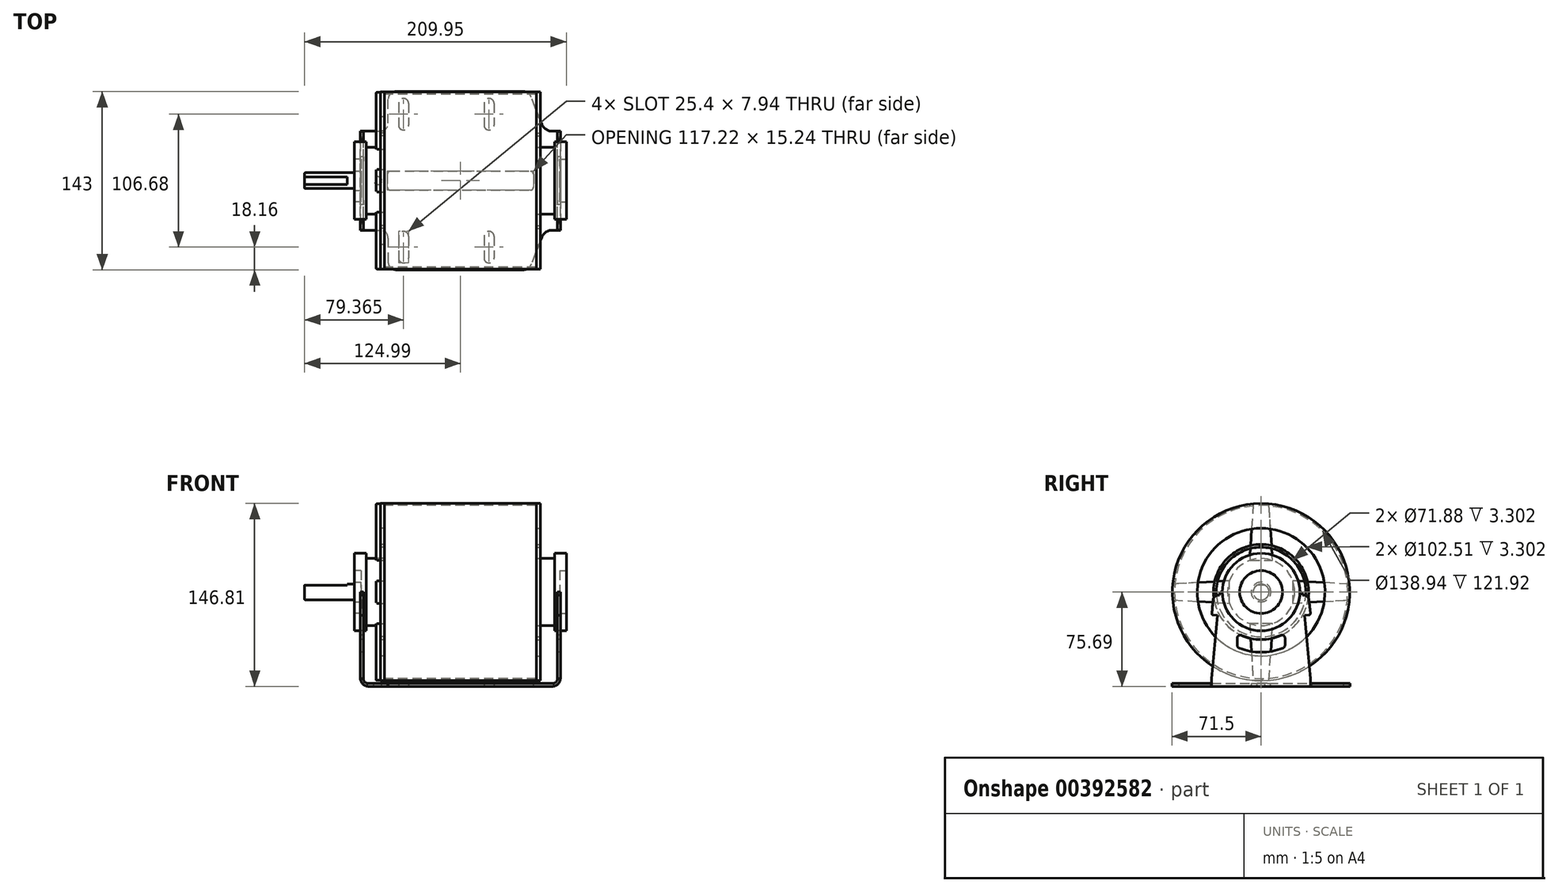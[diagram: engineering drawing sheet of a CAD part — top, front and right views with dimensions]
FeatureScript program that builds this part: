
annotation { "Feature Type Name" : "Feature", "Feature Type Description" : "" }
export const myFeature = defineFeature(function(context is Context, id is Id, definition is map)
    precondition{}
    {
        {
            var Q0;
            Q0=qCreatedBy(makeId("Right.planeOp"),FACE);
            var sketch = newSketch(context, id + "F0", { "sketchPlane" : qUnion([Q0])});
            skCircle(sketch, "E0", {"center": v(0, 0) * mm, "radius": 71.12 * mm});
            skCircle(sketch, "E1.0", {"center": v(0, 0) * mm, "radius": 69.47 * mm});
            skSolve(sketch);
        }
        {
            var Q0;
            Q0=makeQuery(id+"F0.imprint","IMPRINT",FACE,{"disambiguationData":[TD([[makeQuery(id+"F0.imprint","IMPRINT",EDGE,{"derivedFrom":sQuery(id+"F0.wireOp",EDGE,"E0")}),1.0]])]});
            extrude(context, id + "F1", {"entities" : qUnion([Q0]), "depth" : 121.92 * mm});
        }
        {
            var Q0;
            Q0=qCreatedBy(makeId("Front.planeOp"),FACE);
            var sketch = newSketch(context, id + "F2", { "sketchPlane" : qUnion([Q0])});
            skLineSegment(sketch, "E2", {"start": v(0, 0) * mm, "end": v(0, 71.12) * mm});
            skLineSegment(sketch, "E3", {"start": v(0, 71.12) * mm, "end": v(-3.3, 71.12) * mm});
            skLineSegment(sketch, "E4", {"start": v(-3.3, 71.12) * mm, "end": v(-3.3, 26.92) * mm});
            skLineSegment(sketch, "E5", {"start": v(-3.3, 26.92) * mm, "end": v(-14.48, 26.92) * mm});
            skLineSegment(sketch, "E6", {"start": v(-14.48, 26.92) * mm, "end": v(-14.48, 31.12) * mm});
            skLineSegment(sketch, "E7", {"start": v(-14.48, 31.12) * mm, "end": v(-24, 31.12) * mm});
            skLineSegment(sketch, "E8", {"start": v(-24, 31.12) * mm, "end": v(-24, 17.15) * mm});
            skLineSegment(sketch, "E9", {"start": v(-24, 17.15) * mm, "end": v(-18.67, 17.15) * mm});
            skLineSegment(sketch, "E10", {"start": v(-18.67, 17.15) * mm, "end": v(-18.67, 0) * mm});
            skLineSegment(sketch, "E11", {"start": v(-18.67, 0) * mm, "end": v(0, 0) * mm});
            skSolve(sketch);
        }
        {
            var Q0;
            Q0=makeQuery(id+"F2.imprint","IMPRINT",FACE,{"disambiguationData":[TD([[makeQuery(id+"F2.imprint","IMPRINT",EDGE,{"derivedFrom":sQuery(id+"F2.wireOp",EDGE,"E2")}),1.0]])]});
            var Q1;
            Q1=sQuery(id+"F2.wireOp",EDGE,"E11");
            revolve(context, id + "F3", {"entities" : qUnion([Q0]), "axis" : qUnion([Q1]), "revolveType" : RevolveType.FULL});
        }
        {
            var Q0;
            Q0=makeQuery(id+"F3.opRevolve","SWEPT_FACE",FACE,{"disambiguationData":[OSD([sQuery(id+"F2.wireOp",EDGE,"E4")])]});
            var sketch = newSketch(context, id + "F4", { "sketchPlane" : qUnion([Q0])});
            skCircle(sketch, "E12", {"center": v(0, 0) * mm, "radius": 51.26 * mm});
            skCircle(sketch, "E13", {"center": v(0, 0) * mm, "radius": 38.23 * mm});
            skCircle(sketch, "E14.0", {"center": v(0, 0) * mm, "radius": 35.94 * mm});
            skSolve(sketch);
        }
        {
            var Q0;
            Q0=qSketchRegion(id+"F4",true);
            var Q1;
            Q1=makeQuery(id+"F4.imprint","IMPRINT",FACE,{"disambiguationData":[TD([[makeQuery(id+"F4.imprint","IMPRINT",EDGE,{"derivedFrom":sQuery(id+"F4.wireOp",EDGE,"E14.0")}),1.0]])]});
            extrude(context, id + "F5", {"entities" : qUnion([Q0, Q1]), "operationType" : NewBodyOperationType.REMOVE, "endBound" : BoundingType.THROUGH_ALL, "oppositeDirection" : true, "depth" : 25.4 * mm});
        }
        {
            var Q0;
            Q0=qCreatedBy(makeId("Right.planeOp"),FACE);
            var sketch = newSketch(context, id + "F6", { "sketchPlane" : qUnion([Q0])});
            skLineSegment(sketch, "E15", {"start": v(0, 0) * mm, "end": v(0, 71.12) * mm, "construction": true});
            skPoint(sketch, "E16.rect.middle", {"position": v(0, 71.12) * mm});
            skCircle(sketch, "E17", {"center": v(0, 26.92) * mm, "radius": 9.2 * mm, "construction": true});
            skCircle(sketch, "E18.0", {"center": v(0, 0) * mm, "radius": 71.12 * mm, "construction": true});
            skCircle(sketch, "E19", {"center": v(0, 71.12) * mm, "radius": 6.35 * mm, "construction": true});
            skLineSegment(sketch, "E20", {"start": v(9.07, 25.35) * mm, "end": v(6.38, 70.83) * mm});
            skLineSegment(sketch, "E21", {"start": v(6.38, 70.83) * mm, "end": v(-6.38, 70.83) * mm});
            skLineSegment(sketch, "E22", {"start": v(-6.38, 70.83) * mm, "end": v(-9.07, 25.35) * mm});
            skLineSegment(sketch, "E23", {"start": v(-9.07, 25.35) * mm, "end": v(9.07, 25.35) * mm});
            skCircle(sketch, "E24.0", {"center": v(0, 0) * mm, "radius": 26.92 * mm, "construction": true});
            skSolve(sketch);
        }
        {
            var Q0;
            {var subQ3=sQuery(id+"F6.wireOp",EDGE,"E20");Q0=makeQuery(id+"F6.imprint","IMPRINT",FACE,{"disambiguationData":[TD([[makeQuery(id+"F6.imprint","IMPRINT",EDGE,{"derivedFrom":subQ3}),1.0]])]});}
            extrude(context, id + "F7", {"entities" : qUnion([Q0]), "oppositeDirection" : true, "depth" : 6.6 * mm});
        }
        {
            var Q0;
            Q0=makeQuery(id+"F7.opExtrude","CAP_EDGE",EDGE,{"disambiguationData":[OSD([sQuery(id+"F6.wireOp",EDGE,"E20")])],"isStart":false});
            var Q1;
            Q1=makeQuery(id+"F7.opExtrude","CAP_EDGE",EDGE,{"disambiguationData":[OSD([sQuery(id+"F6.wireOp",EDGE,"E21")])],"isStart":false});
            var Q2;
            Q2=makeQuery(id+"F7.opExtrude","CAP_EDGE",EDGE,{"disambiguationData":[OSD([sQuery(id+"F6.wireOp",EDGE,"E22")])],"isStart":false});
            var Q3;
            Q3=makeQuery(id+"F7.opExtrude","SWEPT_EDGE",EDGE,{"disambiguationData":[OSD([sQuery(id+"F2.wireOp",EDGE,"E3"),sQuery(id+"F2.wireOp",EDGE,"E4"),sQuery(id+"F6.wireOp",EDGE,"E20"),sQuery(id+"F6.wireOp",EDGE,"E21")])]});
            var Q4;
            Q4=makeQuery(id+"F7.opExtrude","SWEPT_EDGE",EDGE,{"disambiguationData":[OSD([sQuery(id+"F2.wireOp",EDGE,"E3"),sQuery(id+"F2.wireOp",EDGE,"E4"),sQuery(id+"F6.wireOp",EDGE,"E21"),sQuery(id+"F6.wireOp",EDGE,"E22")])]});
            fillet(context, id + "F8", {"entities" : qUnion([Q0, Q1, Q2, Q3, Q4]), "radius" : 0.5 * mm, "tangentPropagation" : true, "allowEdgeOverflow" : false});
        }
        {
            var Q0;
            Q0=makeQuery(id+"F7.opExtrude","SWEPT_BODY",BODY,{"disambiguationData":[OSD([sQuery(id+"F2.wireOp",EDGE,"E4"),sQuery(id+"F2.wireOp",EDGE,"E5"),sQuery(id+"F6.wireOp",EDGE,"E20"),sQuery(id+"F6.wireOp",EDGE,"E21"),sQuery(id+"F6.wireOp",EDGE,"E22")])]});
            var Q1;
            Q1=sQuery(id+"F2.wireOp",EDGE,"E11");
            circularPattern(context, id + "F9", {"entities" : qUnion([Q0]), "axis" : qUnion([Q1]), "angle" : 360 * degree, "instanceCount" : 4, "equalSpace" : true, "computeTransformsWithoutBuiltin" : true});
        }
        {
            var Q0;
            Q0=qCreatedBy(makeId("Right.planeOp"),FACE);
            cPlane(context, id + "F10", {"entities" : qUnion([Q0]), "cplaneType" : CPlaneType.OFFSET, "offset" : 60.96 * mm, "width" : 152.4 * mm, "height" : 152.4 * mm});
        }
        {
            var Q0;
            Q0=makeQuery(id+"F5.boolean.opBoolean","SPLIT",BODY,{"disambiguationData":[OD(0.0)],"derivedFrom":makeQuery(id+"F3.opRevolve","SWEPT_BODY",BODY,{"disambiguationData":[OSD([sQuery(id+"F2.wireOp",EDGE,"E2"),sQuery(id+"F2.wireOp",EDGE,"E3"),sQuery(id+"F2.wireOp",EDGE,"E4"),sQuery(id+"F2.wireOp",EDGE,"E5"),sQuery(id+"F2.wireOp",EDGE,"E6"),sQuery(id+"F2.wireOp",EDGE,"E7"),sQuery(id+"F2.wireOp",EDGE,"E8"),sQuery(id+"F2.wireOp",EDGE,"E9"),sQuery(id+"F2.wireOp",EDGE,"E10"),sQuery(id+"F2.wireOp",EDGE,"E11")])]})});
            var Q1;
            Q1=qCreatedBy(id+"F10.planeOp",FACE);
            mirror(context, id + "F11", {"entities" : qUnion([Q0]), "mirrorPlane" : qUnion([Q1])});
        }
        {
            var Q0;
            Q0=qCreatedBy(makeId("Front.planeOp"),FACE);
            var sketch = newSketch(context, id + "F12", { "sketchPlane" : qUnion([Q0])});
            skLineSegment(sketch, "E25.0.0", {"start": v(-18.67, -17.15) * mm, "end": v(-18.67, 17.15) * mm, "construction": true});
            skLineSegment(sketch, "E26", {"start": v(-18.67, 0) * mm, "end": v(-64.03, 0) * mm});
            skLineSegment(sketch, "E27", {"start": v(-64.03, 0) * mm, "end": v(-64.03, 5.84) * mm});
            skLineSegment(sketch, "E28", {"start": v(-63.53, 6.35) * mm, "end": v(-23.75, 6.35) * mm});
            skLineSegment(sketch, "E29", {"start": v(-23.24, 7.89) * mm, "end": v(-18.67, 7.89) * mm});
            skLineSegment(sketch, "E30", {"start": v(-18.67, 7.89) * mm, "end": v(-18.67, 0) * mm});
            skLineSegment(sketch, "E31", {"start": v(-23.75, 7.38) * mm, "end": v(-23.75, 6.35) * mm});
            skPoint(sketch, "E32.visualSharp", {"position": v(-23.75, 7.89) * mm});
            skArc(sketch, "E32.filletArc", {"start": v(-23.24, 7.89) * mm, "mid": v(-23.6, 7.74) * mm, "end": v(-23.75, 7.38) * mm});
            skPoint(sketch, "E33.visualSharp", {"position": v(-64.03, 6.35) * mm});
            skArc(sketch, "E33.filletArc", {"start": v(-63.53, 6.35) * mm, "mid": v(-63.88, 6.2) * mm, "end": v(-64.03, 5.84) * mm});
            skSolve(sketch);
        }
        {
            var Q0;
            Q0=makeQuery(id+"F12.imprint","IMPRINT",FACE,{"disambiguationData":[TD([[makeQuery(id+"F12.imprint","IMPRINT",EDGE,{"derivedFrom":sQuery(id+"F12.wireOp",EDGE,"E26")}),-1.0]])]});
            var Q1;
            Q1=sQuery(id+"F12.wireOp",EDGE,"E26");
            revolve(context, id + "F13", {"entities" : qUnion([Q0]), "axis" : qUnion([Q1]), "revolveType" : RevolveType.FULL});
        }
        {
            var Q0;
            Q0=makeQuery(id+"F13.opRevolve","SWEPT_FACE",FACE,{"disambiguationData":[OSD([sQuery(id+"F12.wireOp",EDGE,"E27")])]});
            var sketch = newSketch(context, id + "F14", { "sketchPlane" : qUnion([Q0])});
            skCircle(sketch, "E34.0", {"center": v(0, 0) * mm, "radius": 6.35 * mm});
            skLineSegment(sketch, "E35", {"start": v(-6.6, -6.35) * mm, "end": v(6.6, -6.35) * mm, "construction": true});
            skLineSegment(sketch, "E36", {"start": v(0, -6.35) * mm, "end": v(0, 6.35) * mm, "construction": true});
            skLineSegment(sketch, "E37.0", {"start": v(-3.02, 5.59) * mm, "end": v(3.02, 5.59) * mm});
            skSolve(sketch);
        }
        {
            var Q0;
            {var subQ0=makeQuery(id+"F13.opRevolve","SWEPT_EDGE",EDGE,{"disambiguationData":[OSD([sQuery(id+"F12.wireOp",EDGE,"E27"),sQuery(id+"F12.wireOp",EDGE,"E33.filletArc")])]});var subQ1=sQuery(id+"F14.wireOp",EDGE,"E37.0");var subQ3=makeQuery(id+"F14.imprint","INTERSECT",VERTEX,{"disambiguationData":[OD(0.0)],"derivedFrom":[subQ0,subQ1]});Q0=makeQuery(id+"F14.imprint","IMPRINT",FACE,{"disambiguationData":[TD([[makeQuery(id+"F14.imprint","IMPRINT",EDGE,{"disambiguationData":[TD([[subQ3,-1.0]])],"derivedFrom":subQ1}),1.0]])]});}
            var Q1;
            {var subQ1=sQuery(id+"F14.wireOp",EDGE,"E37.0");var subQ4=sQuery(id+"F14.wireOp",EDGE,"E34.0");var subQ6=makeQuery(id+"F14.imprint","INTERSECT",VERTEX,{"disambiguationData":[OD(0.0)],"derivedFrom":[subQ4,subQ1]});Q1=makeQuery(id+"F14.imprint","IMPRINT",FACE,{"disambiguationData":[TD([[makeQuery(id+"F14.imprint","IMPRINT",EDGE,{"disambiguationData":[TD([[subQ6,1.0]])],"derivedFrom":subQ4}),1.0]])]});}
            extrude(context, id + "F15", {"entities" : qUnion([Q0, Q1]), "operationType" : NewBodyOperationType.REMOVE, "oppositeDirection" : true, "depth" : 34.04 * mm});
        }
        {
            var Q0;
            Q0=qCreatedBy(makeId("Front.planeOp"),FACE);
            var sketch = newSketch(context, id + "F16", { "sketchPlane" : qUnion([Q0])});
            skLineSegment(sketch, "E38", {"start": v(-154.25, 0) * mm, "end": v(252.33, 0) * mm, "construction": true});
            skLineSegment(sketch, "E39", {"start": v(-12.9, -75.7) * mm, "end": v(134.81, -75.7) * mm});
            skLineSegment(sketch, "E40", {"start": v(-24, 31.12) * mm, "end": v(-14.48, 31.12) * mm, "construction": true});
            skLineSegment(sketch, "E41", {"start": v(136.4, 31.12) * mm, "end": v(145.92, 31.12) * mm, "construction": true});
            skLineSegment(sketch, "E42", {"start": v(-19.24, 31.12) * mm, "end": v(-19.24, 0) * mm, "construction": true});
            skLineSegment(sketch, "E43", {"start": v(141.16, 31.12) * mm, "end": v(141.16, 0) * mm, "construction": true});
            skLineSegment(sketch, "E44", {"start": v(-19.24, 0) * mm, "end": v(-19.24, -69.34) * mm});
            skLineSegment(sketch, "E45", {"start": v(141.16, 0) * mm, "end": v(141.16, -69.34) * mm});
            skPoint(sketch, "E46.visualSharp", {"position": v(-19.24, -75.7) * mm});
            skArc(sketch, "E46.filletArc", {"start": v(-19.24, -69.34) * mm, "mid": v(-17.38, -73.83) * mm, "end": v(-12.9, -75.7) * mm});
            skPoint(sketch, "E47.visualSharp", {"position": v(141.16, -75.7) * mm});
            skArc(sketch, "E47.filletArc", {"start": v(134.81, -75.7) * mm, "mid": v(139.3, -73.83) * mm, "end": v(141.16, -69.34) * mm});
            skLineSegment(sketch, "E48.0", {"start": v(138.87, 0) * mm, "end": v(138.87, -69.34) * mm});
            skArc(sketch, "E48.1", {"start": v(134.81, -73.4) * mm, "mid": v(137.68, -72.22) * mm, "end": v(138.87, -69.34) * mm});
            skLineSegment(sketch, "E48.2", {"start": v(-12.9, -73.4) * mm, "end": v(134.81, -73.4) * mm});
            skArc(sketch, "E48.3", {"start": v(-16.95, -69.34) * mm, "mid": v(-15.76, -72.22) * mm, "end": v(-12.9, -73.4) * mm});
            skLineSegment(sketch, "E48.4", {"start": v(-16.95, 0) * mm, "end": v(-16.95, -69.34) * mm});
            skLineSegment(sketch, "E49", {"start": v(-19.24, 0) * mm, "end": v(-16.95, 0) * mm});
            skLineSegment(sketch, "E50", {"start": v(138.87, 0) * mm, "end": v(141.16, 0) * mm});
            skSolve(sketch);
        }
        {
            var Q0;
            Q0=qSketchRegion(id+"F16",true);
            extrude(context, id + "F17", {"entities" : qUnion([Q0]), "depth" : 79.5 * mm, "symmetric" : true});
        }
        {
            var Q0;
            Q0=qCreatedBy(makeId("Top.planeOp"),FACE);
            cPlane(context, id + "F18", {"entities" : qUnion([Q0]), "cplaneType" : CPlaneType.OFFSET, "offset" : 75.7 * mm, "oppositeDirection" : true, "width" : 152.4 * mm, "height" : 152.4 * mm});
        }
        {
            var Q0;
            Q0=qCreatedBy(id+"F18.planeOp",FACE);
            var sketch = newSketch(context, id + "F19", { "sketchPlane" : qUnion([Q0])});
            skLineSegment(sketch, "E51.0", {"start": v(-19.24, -39.75) * mm, "end": v(-12.9, -39.75) * mm, "construction": true});
            skLineSegment(sketch, "E52.0", {"start": v(-19.24, 39.75) * mm, "end": v(-12.9, 39.75) * mm, "construction": true});
            skLineSegment(sketch, "E53.bottom", {"start": v(15.34, 66.04) * mm, "end": v(15.34, 66.04) * mm});
            skLineSegment(sketch, "E53.top", {"start": v(15.34, 40.64) * mm, "end": v(15.34, 40.64) * mm});
            skLineSegment(sketch, "E53.left", {"start": v(11.37, 62.07) * mm, "end": v(11.37, 44.6) * mm});
            skLineSegment(sketch, "E53.right", {"start": v(19.3, 62.07) * mm, "end": v(19.3, 44.6) * mm});
            skPoint(sketch, "E54.visualSharp", {"position": v(11.37, 66.04) * mm});
            skArc(sketch, "E54.filletArc", {"start": v(15.34, 66.04) * mm, "mid": v(12.53, 64.88) * mm, "end": v(11.37, 62.07) * mm});
            skPoint(sketch, "E55.visualSharp", {"position": v(19.3, 66.04) * mm});
            skArc(sketch, "E55.filletArc", {"start": v(19.3, 62.07) * mm, "mid": v(18.14, 64.88) * mm, "end": v(15.34, 66.04) * mm});
            skPoint(sketch, "E56.visualSharp", {"position": v(19.3, 40.64) * mm});
            skArc(sketch, "E56.filletArc", {"start": v(15.34, 40.64) * mm, "mid": v(18.14, 41.8) * mm, "end": v(19.3, 44.6) * mm});
            skPoint(sketch, "E57.visualSharp", {"position": v(11.37, 40.64) * mm});
            skArc(sketch, "E57.filletArc", {"start": v(11.37, 44.6) * mm, "mid": v(12.53, 41.8) * mm, "end": v(15.34, 40.64) * mm});
            skLineSegment(sketch, "E58", {"start": v(2.98, 39.75) * mm, "end": v(2.98, -39.75) * mm, "construction": true});
            skLineSegment(sketch, "E59", {"start": v(-19.24, 0) * mm, "end": v(141.16, 0) * mm, "construction": true});
            skLineSegment(sketch, "E60", {"start": v(9.33, 71.5) * mm, "end": v(111.68, 71.5) * mm});
            skLineSegment(sketch, "E61", {"start": v(9.33, -71.5) * mm, "end": v(111.68, -71.5) * mm});
            skLineSegment(sketch, "E62", {"start": v(2.98, 46.1) * mm, "end": v(2.98, 65.15) * mm});
            skLineSegment(sketch, "E63", {"start": v(2.98, -46.1) * mm, "end": v(2.98, -65.15) * mm});
            skLineSegment(sketch, "E64", {"start": v(-19.24, 39.75) * mm, "end": v(-19.24, -39.75) * mm, "construction": true});
            skLineSegment(sketch, "E65.0", {"start": v(141.16, -39.75) * mm, "end": v(141.16, 39.75) * mm, "construction": true});
            skLineSegment(sketch, "E66", {"start": v(141.16, 39.75) * mm, "end": v(134.81, 39.75) * mm, "construction": true});
            skLineSegment(sketch, "E67", {"start": v(126.25, 45.4) * mm, "end": v(117.6, 67.47) * mm});
            skPoint(sketch, "E68.visualSharp", {"position": v(128.46, 39.75) * mm});
            skArc(sketch, "E68.filletArc", {"start": v(126.25, 45.4) * mm, "mid": v(129.51, 41.3) * mm, "end": v(134.52, 39.75) * mm});
            skPoint(sketch, "E69.visualSharp", {"position": v(2.98, 71.5) * mm});
            skArc(sketch, "E69.filletArc", {"start": v(9.33, 71.5) * mm, "mid": v(4.84, 69.64) * mm, "end": v(2.98, 65.15) * mm});
            skLineSegment(sketch, "E70.0.MirrorCS", {"start": v(141.16, -39.75) * mm, "end": v(134.81, -39.75) * mm, "construction": true});
            skLineSegment(sketch, "E70.1.MirrorCS", {"start": v(126.25, -45.4) * mm, "end": v(117.6, -67.47) * mm});
            skArc(sketch, "E70.2.MirrorCS", {"start": v(126.25, -45.4) * mm, "mid": v(129.51, -41.3) * mm, "end": v(134.52, -39.75) * mm});
            skPoint(sketch, "E71.visualSharp", {"position": v(116.01, 71.5) * mm});
            skArc(sketch, "E71.filletArc", {"start": v(117.6, 67.47) * mm, "mid": v(115.26, 70.4) * mm, "end": v(111.68, 71.5) * mm});
            skPoint(sketch, "E72.visualSharp", {"position": v(116.01, -71.5) * mm});
            skArc(sketch, "E72.filletArc", {"start": v(111.68, -71.5) * mm, "mid": v(115.26, -70.4) * mm, "end": v(117.6, -67.47) * mm});
            skPoint(sketch, "E73.visualSharp", {"position": v(2.98, -71.5) * mm});
            skArc(sketch, "E73.filletArc", {"start": v(2.98, -65.15) * mm, "mid": v(4.84, -69.64) * mm, "end": v(9.33, -71.5) * mm});
            skPoint(sketch, "E74.visualSharp", {"position": v(2.98, 39.75) * mm});
            skArc(sketch, "E74.filletArc", {"start": v(-3.37, 39.75) * mm, "mid": v(1.12, 41.61) * mm, "end": v(2.98, 46.1) * mm});
            skPoint(sketch, "E75.visualSharp", {"position": v(2.98, -39.75) * mm});
            skArc(sketch, "E75.filletArc", {"start": v(2.98, -46.1) * mm, "mid": v(1.12, -41.61) * mm, "end": v(-3.37, -39.75) * mm});
            skArc(sketch, "E76.0.1.0", {"start": v(15.34, -66.04) * mm, "mid": v(18.14, -64.88) * mm, "end": v(19.3, -62.07) * mm});
            skArc(sketch, "E76.0.1.1", {"start": v(11.37, -62.07) * mm, "mid": v(12.53, -64.88) * mm, "end": v(15.34, -66.04) * mm});
            skLineSegment(sketch, "E76.0.1.2", {"start": v(11.37, -44.6) * mm, "end": v(11.37, -62.07) * mm});
            skArc(sketch, "E76.0.1.3", {"start": v(15.34, -40.64) * mm, "mid": v(12.53, -41.8) * mm, "end": v(11.37, -44.6) * mm});
            skArc(sketch, "E76.0.1.4", {"start": v(19.3, -44.6) * mm, "mid": v(18.14, -41.8) * mm, "end": v(15.34, -40.64) * mm});
            skLineSegment(sketch, "E76.0.1.5", {"start": v(19.3, -44.6) * mm, "end": v(19.3, -62.07) * mm});
            skArc(sketch, "E76.1.0.0", {"start": v(83.92, 40.64) * mm, "mid": v(86.72, 41.8) * mm, "end": v(87.88, 44.6) * mm});
            skArc(sketch, "E76.1.0.1", {"start": v(79.95, 44.6) * mm, "mid": v(81.1, 41.8) * mm, "end": v(83.92, 40.64) * mm});
            skLineSegment(sketch, "E76.1.0.2", {"start": v(79.95, 62.07) * mm, "end": v(79.95, 44.6) * mm});
            skArc(sketch, "E76.1.0.3", {"start": v(83.92, 66.04) * mm, "mid": v(81.1, 64.88) * mm, "end": v(79.95, 62.07) * mm});
            skArc(sketch, "E76.1.0.4", {"start": v(87.88, 62.07) * mm, "mid": v(86.72, 64.88) * mm, "end": v(83.92, 66.04) * mm});
            skLineSegment(sketch, "E76.1.0.5", {"start": v(87.88, 62.07) * mm, "end": v(87.88, 44.6) * mm});
            skArc(sketch, "E76.1.1.0", {"start": v(83.92, -66.04) * mm, "mid": v(86.72, -64.88) * mm, "end": v(87.88, -62.07) * mm});
            skArc(sketch, "E76.1.1.1", {"start": v(79.95, -62.07) * mm, "mid": v(81.1, -64.88) * mm, "end": v(83.92, -66.04) * mm});
            skLineSegment(sketch, "E76.1.1.2", {"start": v(79.95, -44.6) * mm, "end": v(79.95, -62.07) * mm});
            skArc(sketch, "E76.1.1.3", {"start": v(83.92, -40.64) * mm, "mid": v(81.1, -41.8) * mm, "end": v(79.95, -44.6) * mm});
            skArc(sketch, "E76.1.1.4", {"start": v(87.88, -44.6) * mm, "mid": v(86.72, -41.8) * mm, "end": v(83.92, -40.64) * mm});
            skLineSegment(sketch, "E76.1.1.5", {"start": v(87.88, -44.6) * mm, "end": v(87.88, -62.07) * mm});
            skLineSegment(sketch, "E76.direction1", {"start": v(15.34, 40.64) * mm, "end": v(83.92, 40.64) * mm, "construction": true});
            skLineSegment(sketch, "E76.direction2", {"start": v(15.34, 40.64) * mm, "end": v(15.34, -66.04) * mm, "construction": true});
            skLineSegment(sketch, "E77.0", {"start": v(-12.9, -39.75) * mm, "end": v(-12.9, 39.75) * mm});
            skLineSegment(sketch, "E78.0", {"start": v(134.81, -39.75) * mm, "end": v(134.81, 39.75) * mm});
            skLineSegment(sketch, "E79", {"start": v(-12.9, 39.75) * mm, "end": v(-3.37, 39.75) * mm});
            skLineSegment(sketch, "E80", {"start": v(-12.9, -39.75) * mm, "end": v(-3.37, -39.75) * mm});
            skLineSegment(sketch, "E81", {"start": v(134.81, 39.75) * mm, "end": v(134.52, 39.75) * mm});
            skLineSegment(sketch, "E82", {"start": v(134.81, -39.75) * mm, "end": v(134.52, -39.75) * mm});
            skSolve(sketch);
        }
        {
            var Q0;
            Q0=makeQuery(id+"F19.imprint","IMPRINT",FACE,{"disambiguationData":[TD([[makeQuery(id+"F19.imprint","IMPRINT",EDGE,{"derivedFrom":sQuery(id+"F19.wireOp",EDGE,"E53.left")}),-1.0]])]});
            extrude(context, id + "F20", {"entities" : qUnion([Q0]), "operationType" : NewBodyOperationType.ADD, "depth" : 2.3 * mm});
        }
        {
            var Q0;
            Q0=makeQuery(id+"F17.opExtrude","SWEPT_FACE",FACE,{"disambiguationData":[OSD([sQuery(id+"F16.wireOp",EDGE,"E44")])]});
            var sketch = newSketch(context, id + "F21", { "sketchPlane" : qUnion([Q0])});
            skArc(sketch, "E83.0", {"start": v(-31.12, 0) * mm, "mid": v(0, -31.12) * mm, "end": v(31.12, 0) * mm});
            skLineSegment(sketch, "E84.0", {"start": v(39.75, -69.34) * mm, "end": v(-39.75, -69.34) * mm});
            skLineSegment(sketch, "E85", {"start": v(31.87, 0) * mm, "end": v(31.12, 0) * mm});
            skLineSegment(sketch, "E86", {"start": v(-33.13, -1.15) * mm, "end": v(-39.75, -69.34) * mm});
            skLineSegment(sketch, "E87", {"start": v(33.13, -1.15) * mm, "end": v(39.75, -69.34) * mm});
            skPoint(sketch, "E88.end.orphan", {"position": v(-39.75, 0) * mm});
            skPoint(sketch, "E89.0.start.orphan", {"position": v(39.75, 0) * mm});
            skLineSegment(sketch, "E90.trimOffspring", {"start": v(-31.12, 0) * mm, "end": v(-31.87, 0) * mm});
            skLineSegment(sketch, "E91", {"start": v(0, 0) * mm, "end": v(0, -69.34) * mm, "construction": true});
            skPoint(sketch, "E92.visualSharp", {"position": v(-33.02, 0) * mm});
            skArc(sketch, "E92.filletArc", {"start": v(-31.87, 0) * mm, "mid": v(-32.72, -0.33) * mm, "end": v(-33.13, -1.15) * mm});
            skPoint(sketch, "E93.visualSharp", {"position": v(33.02, 0) * mm});
            skArc(sketch, "E93.filletArc", {"start": v(33.13, -1.15) * mm, "mid": v(32.72, -0.33) * mm, "end": v(31.87, 0) * mm});
            skLineSegment(sketch, "E94.bottom", {"start": v(33.27, -2.6) * mm, "end": v(33.78, -2.55) * mm});
            skLineSegment(sketch, "E94.top", {"start": v(34.84, -18.78) * mm, "end": v(38.38, -18.44) * mm});
            skLineSegment(sketch, "E94.left", {"start": v(33.27, -2.6) * mm, "end": v(34.84, -18.78) * mm});
            skLineSegment(sketch, "E94.right", {"start": v(38.5, -6.43) * mm, "end": v(39.52, -17.05) * mm});
            skPoint(sketch, "E95.visualSharp", {"position": v(38.08, -2.13) * mm});
            skArc(sketch, "E95.filletArc", {"start": v(38.5, -6.43) * mm, "mid": v(36.94, -3.51) * mm, "end": v(33.78, -2.55) * mm});
            skPoint(sketch, "E96.visualSharp", {"position": v(39.65, -18.31) * mm});
            skArc(sketch, "E96.filletArc", {"start": v(38.38, -18.44) * mm, "mid": v(39.24, -17.98) * mm, "end": v(39.52, -17.05) * mm});
            skLineSegment(sketch, "E97.0.MirrorCS", {"start": v(-33.27, -2.6) * mm, "end": v(-33.78, -2.55) * mm});
            skArc(sketch, "E97.1.MirrorCS", {"start": v(-38.5, -6.43) * mm, "mid": v(-36.94, -3.51) * mm, "end": v(-33.78, -2.55) * mm});
            skLineSegment(sketch, "E97.2.MirrorCS", {"start": v(-34.84, -18.78) * mm, "end": v(-38.38, -18.44) * mm});
            skLineSegment(sketch, "E97.3.MirrorCS", {"start": v(-38.5, -6.43) * mm, "end": v(-39.52, -17.05) * mm});
            skArc(sketch, "E97.4.MirrorCS", {"start": v(-38.38, -18.44) * mm, "mid": v(-39.24, -17.98) * mm, "end": v(-39.52, -17.05) * mm});
            skArc(sketch, "E98", {"start": v(-15.6, -34.76) * mm, "mid": v(0, -38.1) * mm, "end": v(15.6, -34.76) * mm});
            skArc(sketch, "E99.0", {"start": v(-17.57, -44.95) * mm, "mid": v(0, -48.26) * mm, "end": v(17.57, -44.95) * mm});
            skLineSegment(sketch, "E100.rect.left", {"start": v(19.19, -37.07) * mm, "end": v(19.19, -42.58) * mm});
            skLineSegment(sketch, "E100.rect.right", {"start": v(-19.19, -37.07) * mm, "end": v(-19.19, -42.58) * mm});
            skPoint(sketch, "E100.rect.middle", {"position": v(0, -43.18) * mm});
            skPoint(sketch, "E101.orphan", {"position": v(-19.19, -53.44) * mm});
            skPoint(sketch, "E100.rect.top.start.orphan", {"position": v(19.19, -53.44) * mm});
            skPoint(sketch, "E102.visualSharp", {"position": v(-19.19, -44.28) * mm});
            skArc(sketch, "E102.filletArc", {"start": v(-19.19, -42.58) * mm, "mid": v(-18.75, -44.01) * mm, "end": v(-17.57, -44.95) * mm});
            skPoint(sketch, "E103.visualSharp", {"position": v(19.19, -44.28) * mm});
            skArc(sketch, "E103.filletArc", {"start": v(17.57, -44.95) * mm, "mid": v(18.75, -44.01) * mm, "end": v(19.19, -42.58) * mm});
            skPoint(sketch, "E104.visualSharp", {"position": v(19.19, -32.92) * mm});
            skArc(sketch, "E104.filletArc", {"start": v(19.19, -37.07) * mm, "mid": v(18.03, -34.94) * mm, "end": v(15.6, -34.76) * mm});
            skPoint(sketch, "E105.visualSharp", {"position": v(-19.19, -32.92) * mm});
            skArc(sketch, "E105.filletArc", {"start": v(-15.6, -34.76) * mm, "mid": v(-18.03, -34.94) * mm, "end": v(-19.19, -37.07) * mm});
            skSolve(sketch);
        }
        {
            var Q0;
            {var subQ2=sQuery(id+"F21.wireOp",EDGE,"E92.filletArc");Q0=makeQuery(id+"F21.imprint","IMPRINT",FACE,{"disambiguationData":[TD([[makeQuery(id+"F21.imprint","IMPRINT",EDGE,{"derivedFrom":subQ2}),-1.0]])]});}
            var Q1;
            {var subQ2=sQuery(id+"F21.wireOp",EDGE,"E93.filletArc");Q1=makeQuery(id+"F21.imprint","IMPRINT",FACE,{"disambiguationData":[TD([[makeQuery(id+"F21.imprint","IMPRINT",EDGE,{"derivedFrom":subQ2}),-1.0]])]});}
            var Q2;
            {var subQ1=sQuery(id+"F21.wireOp",EDGE,"E83.0");Q2=makeQuery(id+"F21.imprint","IMPRINT",FACE,{"disambiguationData":[TD([[makeQuery(id+"F21.imprint","IMPRINT",EDGE,{"derivedFrom":subQ1}),1.0]])]});}
            var Q3;
            Q3=makeQuery(id+"F21.imprint","IMPRINT",FACE,{"disambiguationData":[TD([[makeQuery(id+"F21.imprint","IMPRINT",EDGE,{"derivedFrom":sQuery(id+"F21.wireOp",EDGE,"E98")}),-1.0]])]});
            extrude(context, id + "F22", {"entities" : qUnion([Q0, Q1, Q2, Q3]), "oppositeDirection" : true, "depth" : 160.4 * mm});
        }
        {
            var Q0;
            Q0=makeQuery(id+"F22.opExtrude","SWEPT_BODY",BODY,{"disambiguationData":[OSD([sQuery(id+"F16.wireOp",EDGE,"E44"),sQuery(id+"F16.wireOp",EDGE,"E49"),sQuery(id+"F21.wireOp",EDGE,"E83.0")])]});
            var Q1;
            Q1=makeQuery(id+"F22.opExtrude","SWEPT_BODY",BODY,{"disambiguationData":[OSD([sQuery(id+"F16.wireOp",EDGE,"E44"),sQuery(id+"F16.wireOp",EDGE,"E49"),sQuery(id+"F21.wireOp",EDGE,"E86"),sQuery(id+"F21.wireOp",EDGE,"E92.filletArc"),sQuery(id+"F21.wireOp",EDGE,"E97.0.MirrorCS"),sQuery(id+"F21.wireOp",EDGE,"E97.1.MirrorCS"),sQuery(id+"F21.wireOp",EDGE,"E97.2.MirrorCS"),sQuery(id+"F21.wireOp",EDGE,"E97.3.MirrorCS"),sQuery(id+"F21.wireOp",EDGE,"E97.4.MirrorCS")])]});
            var Q2;
            Q2=makeQuery(id+"F22.opExtrude","SWEPT_BODY",BODY,{"disambiguationData":[OSD([sQuery(id+"F16.wireOp",EDGE,"E44"),sQuery(id+"F16.wireOp",EDGE,"E49"),sQuery(id+"F21.wireOp",EDGE,"E87"),sQuery(id+"F21.wireOp",EDGE,"E93.filletArc"),sQuery(id+"F21.wireOp",EDGE,"E94.bottom"),sQuery(id+"F21.wireOp",EDGE,"E94.top"),sQuery(id+"F21.wireOp",EDGE,"E94.right"),sQuery(id+"F21.wireOp",EDGE,"E95.filletArc"),sQuery(id+"F21.wireOp",EDGE,"E96.filletArc")])]});
            var Q3;
            Q3=makeQuery(id+"F22.opExtrude","SWEPT_BODY",BODY,{"disambiguationData":[OSD([sQuery(id+"F21.wireOp",EDGE,"E98"),sQuery(id+"F21.wireOp",EDGE,"E99.0"),sQuery(id+"F21.wireOp",EDGE,"E100.rect.left"),sQuery(id+"F21.wireOp",EDGE,"E100.rect.right"),sQuery(id+"F21.wireOp",EDGE,"E102.filletArc"),sQuery(id+"F21.wireOp",EDGE,"E103.filletArc"),sQuery(id+"F21.wireOp",EDGE,"E104.filletArc"),sQuery(id+"F21.wireOp",EDGE,"E105.filletArc")])]});
            var Q4;
            Q4=makeQuery(id+"F17.opExtrude","SWEPT_BODY",BODY,{"disambiguationData":[OSD([sQuery(id+"F16.wireOp",EDGE,"E39"),sQuery(id+"F16.wireOp",EDGE,"E44"),sQuery(id+"F16.wireOp",EDGE,"E45"),sQuery(id+"F16.wireOp",EDGE,"E46.filletArc"),sQuery(id+"F16.wireOp",EDGE,"E47.filletArc"),sQuery(id+"F16.wireOp",EDGE,"E48.0"),sQuery(id+"F16.wireOp",EDGE,"E48.1"),sQuery(id+"F16.wireOp",EDGE,"E48.2"),sQuery(id+"F16.wireOp",EDGE,"E48.3"),sQuery(id+"F16.wireOp",EDGE,"E48.4"),sQuery(id+"F16.wireOp",EDGE,"E49"),sQuery(id+"F16.wireOp",EDGE,"E50")])]});
            booleanBodies(context, id + "F23", {"operationType" : BooleanOperationType.SUBTRACTION, "tools" : qUnion([Q0, Q1, Q2, Q3]), "targets" : qUnion([Q4])});
        }
        {
            var Q0;
            Q0=makeQuery(id+"F20.boolean.opBoolean","MERGE",FACE,{"derivedFrom":[makeQuery(id+"F17.opExtrude","SWEPT_FACE",FACE,{"disambiguationData":[OSD([sQuery(id+"F16.wireOp",EDGE,"E48.2")])]}),makeQuery(id+"F20.opExtrude","CAP_FACE",FACE,{"disambiguationData":[OSD([sQuery(id+"F19.wireOp",EDGE,"E53.left"),sQuery(id+"F19.wireOp",EDGE,"E53.right"),sQuery(id+"F19.wireOp",EDGE,"E54.filletArc"),sQuery(id+"F19.wireOp",EDGE,"E55.filletArc"),sQuery(id+"F19.wireOp",EDGE,"E56.filletArc"),sQuery(id+"F19.wireOp",EDGE,"E57.filletArc"),sQuery(id+"F19.wireOp",EDGE,"E60"),sQuery(id+"F19.wireOp",EDGE,"E61"),sQuery(id+"F19.wireOp",EDGE,"E62"),sQuery(id+"F19.wireOp",EDGE,"E63"),sQuery(id+"F19.wireOp",EDGE,"E67"),sQuery(id+"F19.wireOp",EDGE,"E68.filletArc"),sQuery(id+"F19.wireOp",EDGE,"E69.filletArc"),sQuery(id+"F19.wireOp",EDGE,"E70.1.MirrorCS"),sQuery(id+"F19.wireOp",EDGE,"E70.2.MirrorCS"),sQuery(id+"F19.wireOp",EDGE,"E71.filletArc"),sQuery(id+"F19.wireOp",EDGE,"E72.filletArc"),sQuery(id+"F19.wireOp",EDGE,"E73.filletArc"),sQuery(id+"F19.wireOp",EDGE,"E74.filletArc"),sQuery(id+"F19.wireOp",EDGE,"E75.filletArc"),sQuery(id+"F19.wireOp",EDGE,"E76.0.1.0"),sQuery(id+"F19.wireOp",EDGE,"E76.0.1.1"),sQuery(id+"F19.wireOp",EDGE,"E76.0.1.2"),sQuery(id+"F19.wireOp",EDGE,"E76.0.1.3"),sQuery(id+"F19.wireOp",EDGE,"E76.0.1.4"),sQuery(id+"F19.wireOp",EDGE,"E76.0.1.5"),sQuery(id+"F19.wireOp",EDGE,"E76.1.0.0"),sQuery(id+"F19.wireOp",EDGE,"E76.1.0.1"),sQuery(id+"F19.wireOp",EDGE,"E76.1.0.2"),sQuery(id+"F19.wireOp",EDGE,"E76.1.0.3"),sQuery(id+"F19.wireOp",EDGE,"E76.1.0.4"),sQuery(id+"F19.wireOp",EDGE,"E76.1.0.5"),sQuery(id+"F19.wireOp",EDGE,"E76.1.1.0"),sQuery(id+"F19.wireOp",EDGE,"E76.1.1.1"),sQuery(id+"F19.wireOp",EDGE,"E76.1.1.2"),sQuery(id+"F19.wireOp",EDGE,"E76.1.1.3"),sQuery(id+"F19.wireOp",EDGE,"E76.1.1.4"),sQuery(id+"F19.wireOp",EDGE,"E76.1.1.5"),sQuery(id+"F19.wireOp",EDGE,"E77.0"),sQuery(id+"F19.wireOp",EDGE,"E78.0"),sQuery(id+"F19.wireOp",EDGE,"E79"),sQuery(id+"F19.wireOp",EDGE,"E80"),sQuery(id+"F19.wireOp",EDGE,"E81"),sQuery(id+"F19.wireOp",EDGE,"E82")])],"isStart":false})]});
            var sketch = newSketch(context, id + "F24", { "sketchPlane" : qUnion([Q0])});
            skLineSegment(sketch, "E106.0", {"start": v(-12.9, -39.75) * mm, "end": v(-12.9, 39.75) * mm, "construction": true});
            skLineSegment(sketch, "E107.0", {"start": v(134.81, -39.75) * mm, "end": v(134.81, 39.75) * mm, "construction": true});
            skLineSegment(sketch, "E108.rect.bottom", {"start": v(4.89, 7.62) * mm, "end": v(117.03, 7.62) * mm});
            skLineSegment(sketch, "E108.rect.top", {"start": v(4.89, -7.62) * mm, "end": v(117.03, -7.62) * mm});
            skLineSegment(sketch, "E108.rect.left", {"start": v(2.35, 5.08) * mm, "end": v(2.35, -5.08) * mm});
            skLineSegment(sketch, "E108.rect.right", {"start": v(119.57, 5.08) * mm, "end": v(119.57, -5.08) * mm});
            skPoint(sketch, "E108.rect.middle", {"position": v(60.96, 0) * mm});
            skLineSegment(sketch, "E109", {"start": v(2.35, 0) * mm, "end": v(-12.9, 0) * mm, "construction": true});
            skLineSegment(sketch, "E110", {"start": v(119.57, 0) * mm, "end": v(134.81, 0) * mm, "construction": true});
            skCircle(sketch, "E111", {"center": v(-5.27, 0) * mm, "radius": 3.18 * mm});
            skLineSegment(sketch, "E112", {"start": v(60.96, 7.62) * mm, "end": v(60.96, -7.62) * mm, "construction": true});
            skCircle(sketch, "E113.0.MirrorC", {"center": v(127.2, 0) * mm, "radius": 3.18 * mm});
            skPoint(sketch, "E114.visualSharp", {"position": v(2.35, 7.62) * mm});
            skArc(sketch, "E114.filletArc", {"start": v(4.89, 7.62) * mm, "mid": v(3.1, 6.88) * mm, "end": v(2.35, 5.08) * mm});
            skPoint(sketch, "E115.visualSharp", {"position": v(119.57, 7.62) * mm});
            skArc(sketch, "E115.filletArc", {"start": v(119.57, 5.08) * mm, "mid": v(118.83, 6.88) * mm, "end": v(117.03, 7.62) * mm});
            skPoint(sketch, "E116.visualSharp", {"position": v(119.57, -7.62) * mm});
            skArc(sketch, "E116.filletArc", {"start": v(117.03, -7.62) * mm, "mid": v(118.83, -6.88) * mm, "end": v(119.57, -5.08) * mm});
            skPoint(sketch, "E117.visualSharp", {"position": v(2.35, -7.62) * mm});
            skArc(sketch, "E117.filletArc", {"start": v(2.35, -5.08) * mm, "mid": v(3.1, -6.88) * mm, "end": v(4.89, -7.62) * mm});
            skSolve(sketch);
        }
        {
            var Q0;
            Q0=makeQuery(id+"F24.imprint","IMPRINT",FACE,{"disambiguationData":[TD([[makeQuery(id+"F24.imprint","IMPRINT",EDGE,{"derivedFrom":sQuery(id+"F24.wireOp",EDGE,"E111")}),1.0]])]});
            var Q1;
            Q1=makeQuery(id+"F24.imprint","IMPRINT",FACE,{"disambiguationData":[TD([[makeQuery(id+"F24.imprint","IMPRINT",EDGE,{"derivedFrom":sQuery(id+"F24.wireOp",EDGE,"E108.rect.bottom")}),-1.0]])]});
            var Q2;
            Q2=makeQuery(id+"F24.imprint","IMPRINT",FACE,{"disambiguationData":[TD([[makeQuery(id+"F24.imprint","IMPRINT",EDGE,{"derivedFrom":sQuery(id+"F24.wireOp",EDGE,"E113.0.MirrorC")}),-1.0]])]});
            extrude(context, id + "F25", {"entities" : qUnion([Q0, Q1, Q2]), "operationType" : NewBodyOperationType.REMOVE, "endBound" : BoundingType.THROUGH_ALL, "oppositeDirection" : true, "depth" : 25.4 * mm});
        }
    });
